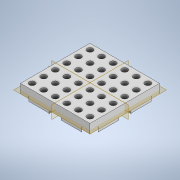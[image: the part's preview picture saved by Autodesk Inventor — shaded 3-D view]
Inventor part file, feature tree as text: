
AUTODESK INVENTOR PART (.ipt)
format: ipt  version: 2022.4 (Build 264492010, 492A)  size: 300,032 bytes
history: native  units: mm
features: extrude x4, sketch x2
ambient origin geometry x8: Origin, YZ Plane, XZ Plane, XY Plane, X Axis, Y Axis, Z Axis, Center Point
bodies: Solid1 (feature_tree)
feature tree (6):
  extrude  "Extrusion1"  Depth=60.0mm
  extrude  "Extrusion2"  Depth=10.0mm
  extrude  "Extrusion3"  Depth=8.0mm
  extrude  "Extrusion4"  Depth=3.0mm
  sketch  "Sketch1"  dims[d0=60.0mm d1=60.0mm]
  sketch  "Sketch3"  dims[d2=10.0mm d3=0.0mm d4=10.0mm d5=8.0mm d6=3.0mm d7=40.0mm d9=360.0deg d11=2.0mm d12=0.0mm d13=4.0mm d14=0.0mm d15=5.0mm d16=5.0mm d17=5.0mm d18=60.0mm d20=10.0mm d21=60.0mm d23=10.0mm d26=5.0mm d27=0.0mm d33=135.0deg d34=5.0mm d35=5.0mm d37=8.0mm d38=3.0mm d39=7.071068mm d40=5.0mm d41=40.0mm d43=360.0deg]
